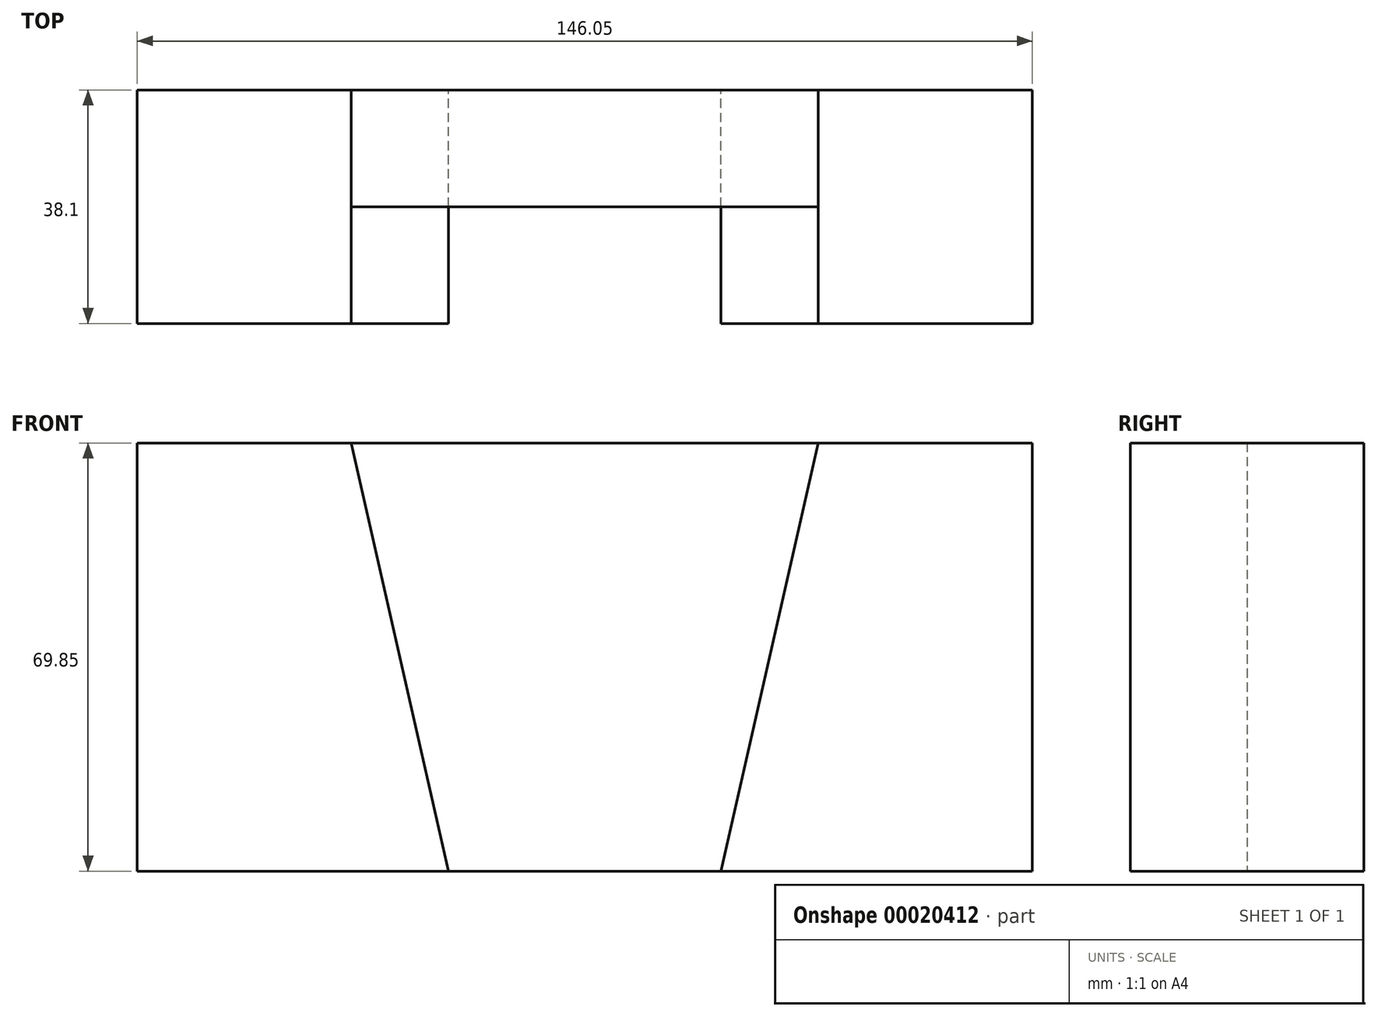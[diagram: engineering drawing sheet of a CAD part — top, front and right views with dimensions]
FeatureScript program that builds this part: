
annotation { "Feature Type Name" : "Feature", "Feature Type Description" : "" }
export const myFeature = defineFeature(function(context is Context, id is Id, definition is map)
    precondition{}
    {
        {
            var Q0;
            Q0=qCreatedBy(makeId("Front.planeOp"),FACE);
            var sketch = newSketch(context, id + "F0", { "sketchPlane" : qUnion([Q0])});
            skLineSegment(sketch, "E0.bottom", {"start": v(-72.8, 35.55) * mm, "end": v(73.25, 35.55) * mm});
            skLineSegment(sketch, "E0.top", {"start": v(-72.8, -34.3) * mm, "end": v(73.25, -34.3) * mm});
            skLineSegment(sketch, "E0.left", {"start": v(-72.8, 35.55) * mm, "end": v(-72.8, -34.3) * mm});
            skLineSegment(sketch, "E0.right", {"start": v(73.25, 35.55) * mm, "end": v(73.25, -34.3) * mm});
            skLineSegment(sketch, "E1", {"start": v(-37.87, 35.55) * mm, "end": v(-22, -34.3) * mm});
            skLineSegment(sketch, "E2", {"start": v(38.33, 35.55) * mm, "end": v(22.45, -34.3) * mm});
            skSolve(sketch);
        }
        {
            var Q0;
            {var subQ1=sQuery(id+"F0.wireOp",EDGE,"E0.left");Q0=makeQuery(id+"F0.imprint","IMPRINT",FACE,{"disambiguationData":[TD([[makeQuery(id+"F0.imprint","IMPRINT",EDGE,{"derivedFrom":subQ1}),1.0]])]});}
            extrude(context, id + "F1", {"entities" : qUnion([Q0]), "depth" : 38.1 * mm});
        }
        {
            var Q0;
            {var subQ1=sQuery(id+"F0.wireOp",EDGE,"E0.right");Q0=makeQuery(id+"F0.imprint","IMPRINT",FACE,{"disambiguationData":[TD([[makeQuery(id+"F0.imprint","IMPRINT",EDGE,{"derivedFrom":subQ1}),-1.0]])]});}
            extrude(context, id + "F2", {"entities" : qUnion([Q0]), "depth" : 38.1 * mm});
        }
        {
            var Q0;
            {var subQ1=sQuery(id+"F0.wireOp",EDGE,"E1");Q0=makeQuery(id+"F0.imprint","IMPRINT",FACE,{"disambiguationData":[TD([[makeQuery(id+"F0.imprint","IMPRINT",EDGE,{"derivedFrom":subQ1}),1.0]])]});}
            extrude(context, id + "F3", {"entities" : qUnion([Q0]), "depth" : 19.05 * mm});
        }
    });
